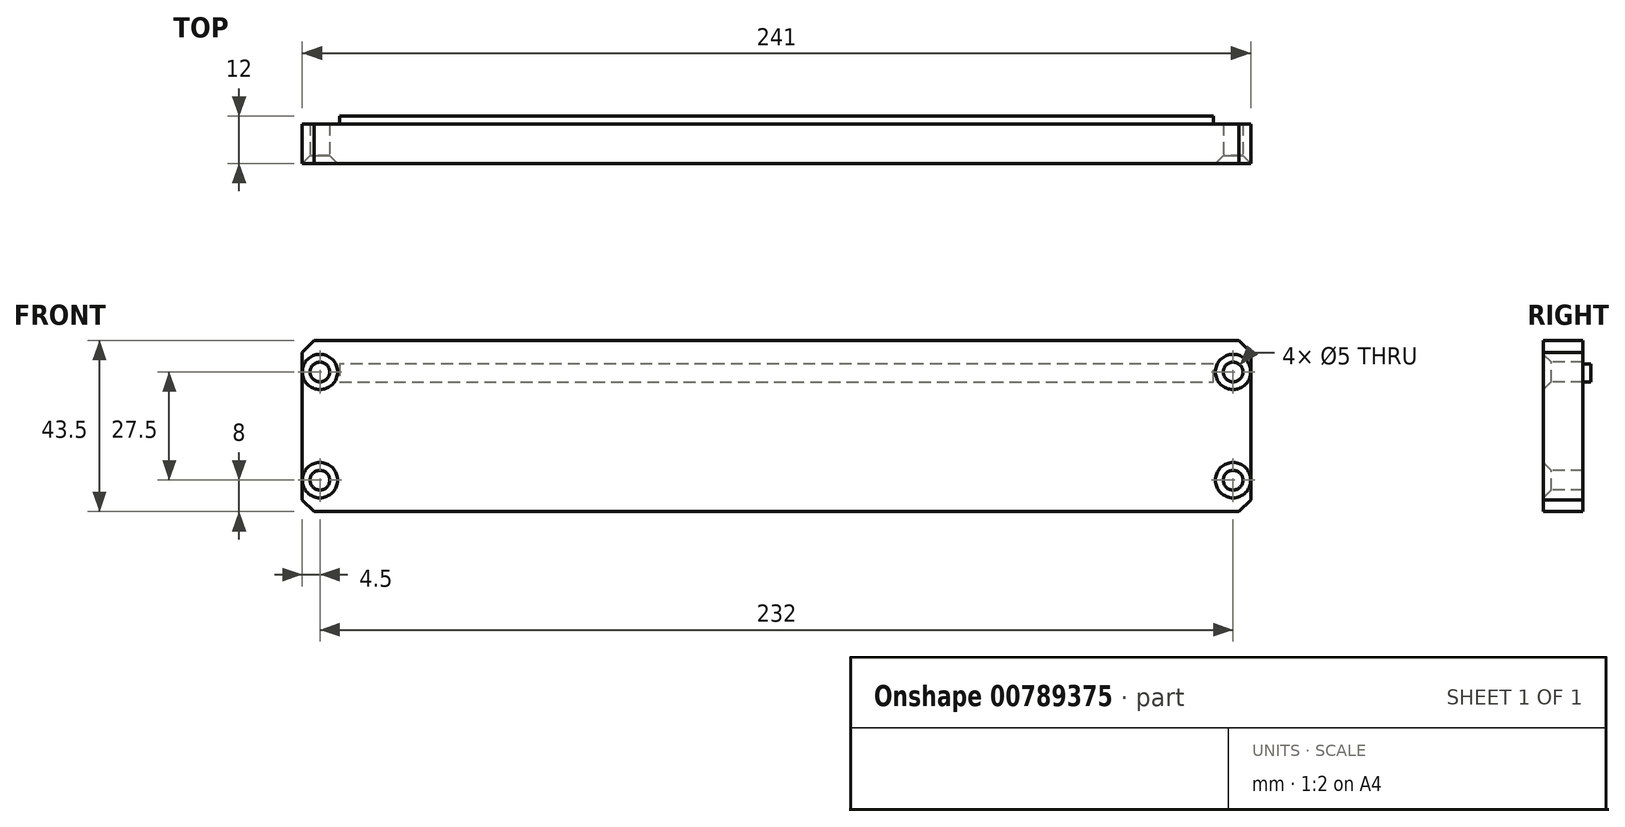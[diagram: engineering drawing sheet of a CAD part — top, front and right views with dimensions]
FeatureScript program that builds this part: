
annotation { "Feature Type Name" : "Feature", "Feature Type Description" : "" }
export const myFeature = defineFeature(function(context is Context, id is Id, definition is map)
    precondition{}
    {
        {
            var Q0;
            Q0=qCreatedBy(makeId("Front.planeOp"),FACE);
            var sketch = newSketch(context, id + "F0", { "sketchPlane" : qUnion([Q0])});
            skLineSegment(sketch, "E0", {"start": v(0, 0) * mm, "end": v(241, 0) * mm});
            skLineSegment(sketch, "E1", {"start": v(241, 0) * mm, "end": v(241, 43.5) * mm});
            skLineSegment(sketch, "E2", {"start": v(241, 43.5) * mm, "end": v(0, 43.5) * mm});
            skLineSegment(sketch, "E3", {"start": v(0, 43.5) * mm, "end": v(0, 0) * mm});
            skSolve(sketch);
        }
        {
            var Q0;
            Q0=makeQuery(id+"F0.imprint","IMPRINT",FACE,{"disambiguationData":[TD([[makeQuery(id+"F0.imprint","IMPRINT",EDGE,{"derivedFrom":sQuery(id+"F0.wireOp",EDGE,"E0")}),1.0]])]});
            extrude(context, id + "F1", {"entities" : qUnion([Q0]), "depth" : 10 * mm, "offsetDistance" : 25 * mm});
        }
        {
            var Q0;
            Q0=makeQuery(id+"F1.opExtrude","SWEPT_EDGE",EDGE,{"disambiguationData":[OSD([sQuery(id+"F0.wireOp",EDGE,"E1"),sQuery(id+"F0.wireOp",EDGE,"E2")])]});
            var Q1;
            Q1=makeQuery(id+"F1.opExtrude","SWEPT_EDGE",EDGE,{"disambiguationData":[OSD([sQuery(id+"F0.wireOp",EDGE,"E0"),sQuery(id+"F0.wireOp",EDGE,"E1")])]});
            var Q2;
            Q2=makeQuery(id+"F1.opExtrude","SWEPT_EDGE",EDGE,{"disambiguationData":[OSD([sQuery(id+"F0.wireOp",EDGE,"E2"),sQuery(id+"F0.wireOp",EDGE,"E3")])]});
            var Q3;
            Q3=makeQuery(id+"F1.opExtrude","SWEPT_EDGE",EDGE,{"disambiguationData":[OSD([sQuery(id+"F0.wireOp",EDGE,"E0"),sQuery(id+"F0.wireOp",EDGE,"E3")])]});
            chamfer(context, id + "F2", {"entities" : qUnion([Q0, Q1, Q2, Q3]), "width" : 3 * mm, "tangentPropagation" : true});
        }
        {
            var Q0;
            Q0=makeQuery(id+"F1.opExtrude","CAP_FACE",FACE,{"disambiguationData":[OSD([sQuery(id+"F0.wireOp",EDGE,"E0"),sQuery(id+"F0.wireOp",EDGE,"E1"),sQuery(id+"F0.wireOp",EDGE,"E2"),sQuery(id+"F0.wireOp",EDGE,"E3")])],"isStart":true});
            var sketch = newSketch(context, id + "F3", { "sketchPlane" : qUnion([Q0])});
            skLineSegment(sketch, "E4", {"start": v(-9.5, 37.5) * mm, "end": v(-9.5, 33) * mm});
            skLineSegment(sketch, "E5", {"start": v(-9.5, 33) * mm, "end": v(-231.5, 33) * mm});
            skLineSegment(sketch, "E6", {"start": v(-231.5, 33) * mm, "end": v(-231.5, 37.5) * mm});
            skLineSegment(sketch, "E7", {"start": v(-231.5, 37.5) * mm, "end": v(-9.5, 37.5) * mm});
            skSolve(sketch);
        }
        {
            var Q0;
            Q0 = qSketchRegion(id + "F3", true);
            extrude(context, id + "F4", {"entities" : qUnion([Q0]), "operationType" : NewBodyOperationType.ADD, "depth" : 2 * mm, "offsetDistance" : 25 * mm});
        }
        {
            var Q0;
            Q0=makeQuery(id+"F1.opExtrude","CAP_FACE",FACE,{"disambiguationData":[OSD([sQuery(id+"F0.wireOp",EDGE,"E0"),sQuery(id+"F0.wireOp",EDGE,"E1"),sQuery(id+"F0.wireOp",EDGE,"E2"),sQuery(id+"F0.wireOp",EDGE,"E3")])],"isStart":false});
            var sketch = newSketch(context, id + "F5", { "sketchPlane" : qUnion([Q0])});
            skPoint(sketch, "E8", {"position": v(4.5, 8) * mm});
            skPoint(sketch, "E9", {"position": v(4.5, 35.5) * mm});
            skPoint(sketch, "E10", {"position": v(236.5, 35.5) * mm});
            skPoint(sketch, "E11", {"position": v(236.5, 8) * mm});
            skSolve(sketch);
        }
        {
            var Q0;
            Q0=sQuery(id+"F5.wireOp",VERTEX,"E10");
            var Q1;
            Q1=sQuery(id+"F5.wireOp",VERTEX,"E11");
            var Q2;
            Q2=sQuery(id+"F5.wireOp",VERTEX,"E9");
            var Q3;
            Q3=sQuery(id+"F5.wireOp",VERTEX,"E8");
            var Q4;
            Q4=makeQuery(id+"F1.opExtrude","SWEPT_BODY",BODY,{"disambiguationData":[OSD([sQuery(id+"F0.wireOp",EDGE,"E0"),sQuery(id+"F0.wireOp",EDGE,"E1"),sQuery(id+"F0.wireOp",EDGE,"E2"),sQuery(id+"F0.wireOp",EDGE,"E3")])]});
            hole(context, id + "F6", {"style" : HoleStyle.C_SINK, "endStyle" : HoleEndStyle.THROUGH, "standardTappedOrClearance" : lookupTablePath({ "standard" : "ISO", "size" : "5", "type" : "Drilled" }), "standardBlindInLast" : lookupTablePath({ "standard" : "ISO", "size" : "5", "type" : "Drilled" }), "holeDiameter" : 5 * mm, "cSinkDiameter" : 8.96 * mm, "cSinkAngle" : 90 * degree, "majorDiameter" : 5 * mm, "isTappedThrough" : true, "tappedDepth" : 12 * mm, "tapClearance" : 3, "locations" : qUnion([Q0, Q1, Q2, Q3]), "scope" : qUnion([Q4])});
        }
    });
